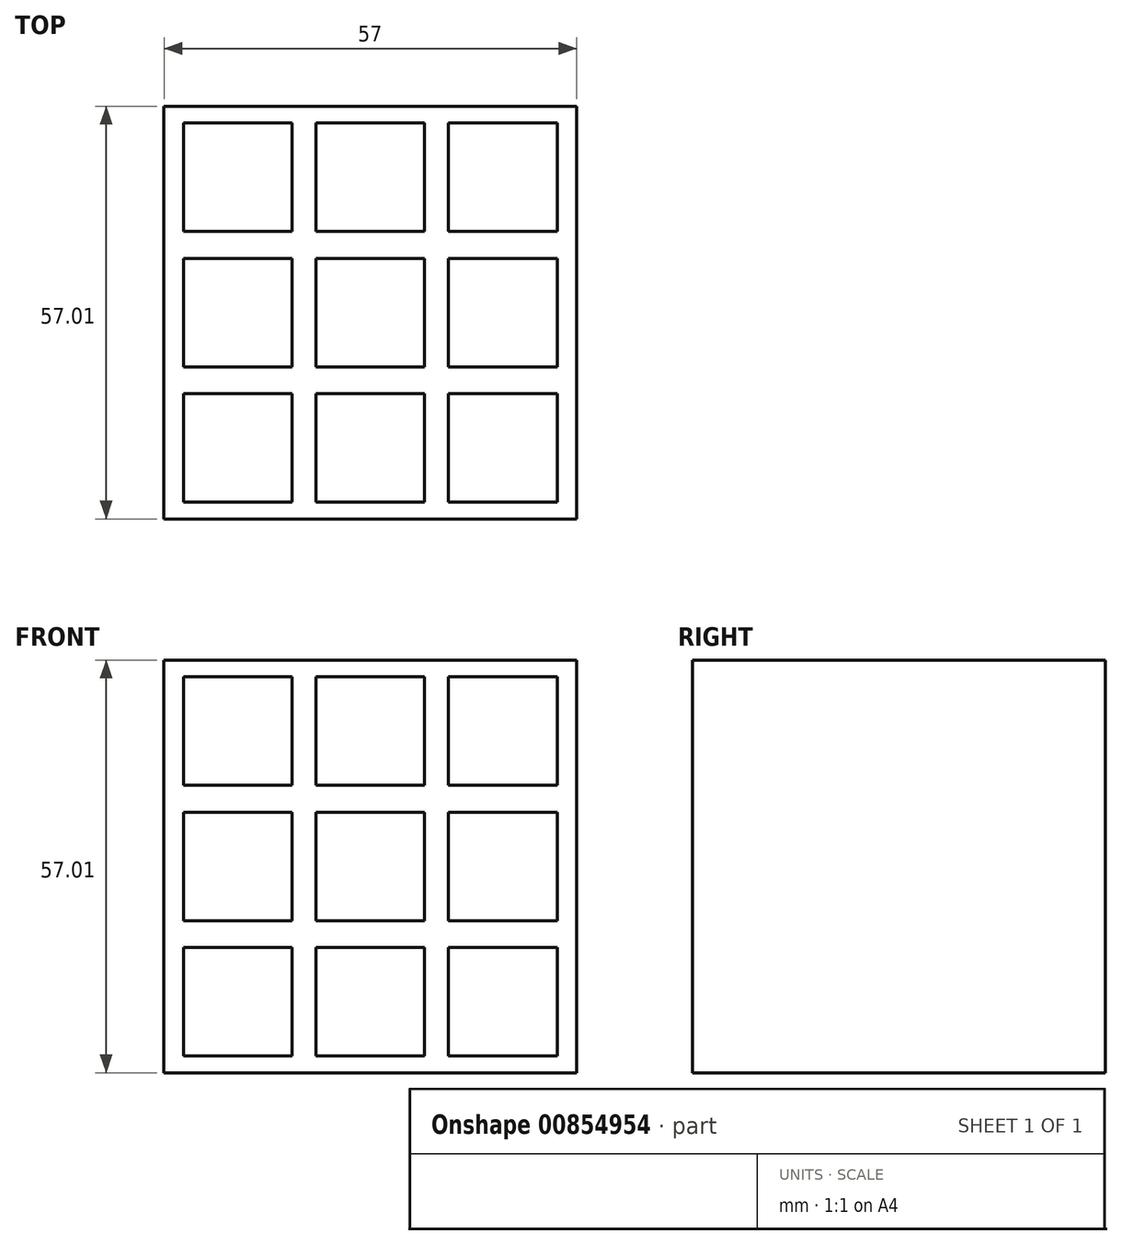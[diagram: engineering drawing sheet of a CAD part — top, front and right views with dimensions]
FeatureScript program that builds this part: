
annotation { "Feature Type Name" : "Feature", "Feature Type Description" : "" }
export const myFeature = defineFeature(function(context is Context, id is Id, definition is map)
    precondition{}
    {
        {
            var Q0;
            Q0=qCreatedBy(makeId("Front.planeOp"),FACE);
            var sketch = newSketch(context, id + "F0", { "sketchPlane" : qUnion([Q0])});
            skLineSegment(sketch, "E0.bottom", {"start": v(-57.56, 22.9) * mm, "end": v(-0.56, 22.9) * mm});
            skLineSegment(sketch, "E0.top", {"start": v(-57.56, -34.1) * mm, "end": v(-0.56, -34.1) * mm});
            skLineSegment(sketch, "E0.left", {"start": v(-57.56, 22.9) * mm, "end": v(-57.56, -34.1) * mm});
            skLineSegment(sketch, "E0.right", {"start": v(-0.56, 22.9) * mm, "end": v(-0.56, -34.1) * mm});
            skSolve(sketch);
        }
        {
            var Q0;
            Q0=qSketchRegion(id+"F0",true);
            extrude(context, id + "F1", {"entities" : qUnion([Q0]), "depth" : 57 * mm, "offsetDistance" : 25 * mm});
        }
        {
            var Q0;
            Q0=makeQuery(id+"F1.opExtrude","SWEPT_FACE",FACE,{"disambiguationData":[OSD([sQuery(id+"F0.wireOp",EDGE,"E0.bottom")])]});
            var sketch = newSketch(context, id + "F2", { "sketchPlane" : qUnion([Q0])});
            skLineSegment(sketch, "E1.bottom", {"start": v(-3.26, -2.3) * mm, "end": v(-18.26, -2.3) * mm});
            skLineSegment(sketch, "E1.top", {"start": v(-3.26, -17.3) * mm, "end": v(-18.26, -17.3) * mm});
            skLineSegment(sketch, "E1.left", {"start": v(-3.26, -2.3) * mm, "end": v(-3.26, -17.3) * mm});
            skLineSegment(sketch, "E1.right", {"start": v(-18.26, -2.3) * mm, "end": v(-18.26, -17.3) * mm});
            skLineSegment(sketch, "E2.bottom", {"start": v(-3.26, -21) * mm, "end": v(-18.26, -21) * mm});
            skLineSegment(sketch, "E2.top", {"start": v(-3.26, -36) * mm, "end": v(-18.26, -36) * mm});
            skLineSegment(sketch, "E2.left", {"start": v(-3.26, -21) * mm, "end": v(-3.26, -36) * mm});
            skLineSegment(sketch, "E2.right", {"start": v(-18.26, -21) * mm, "end": v(-18.26, -36) * mm});
            skLineSegment(sketch, "E3.bottom", {"start": v(-3.26, -39.7) * mm, "end": v(-18.26, -39.7) * mm});
            skLineSegment(sketch, "E3.top", {"start": v(-3.26, -54.7) * mm, "end": v(-18.26, -54.7) * mm});
            skLineSegment(sketch, "E3.left", {"start": v(-3.26, -39.7) * mm, "end": v(-3.26, -54.7) * mm});
            skLineSegment(sketch, "E3.right", {"start": v(-18.26, -39.7) * mm, "end": v(-18.26, -54.7) * mm});
            skLineSegment(sketch, "E4", {"start": v(-19.91, -57) * mm, "end": v(-19.91, 0) * mm});
            skLineSegment(sketch, "E5.MirrorCS", {"start": v(-36.56, -39.7) * mm, "end": v(-21.56, -39.7) * mm});
            skLineSegment(sketch, "E6.MirrorCS", {"start": v(-21.56, -39.7) * mm, "end": v(-21.56, -54.7) * mm});
            skLineSegment(sketch, "E7.MirrorCS", {"start": v(-36.56, -54.7) * mm, "end": v(-21.56, -54.7) * mm});
            skLineSegment(sketch, "E8.MirrorCS", {"start": v(-36.56, -39.7) * mm, "end": v(-36.56, -54.7) * mm});
            skLineSegment(sketch, "E9.MirrorCS", {"start": v(-36.56, -36) * mm, "end": v(-21.56, -36) * mm});
            skLineSegment(sketch, "E10.MirrorCS", {"start": v(-21.56, -21) * mm, "end": v(-21.56, -36) * mm});
            skLineSegment(sketch, "E11.MirrorCS", {"start": v(-36.56, -21) * mm, "end": v(-21.56, -21) * mm});
            skLineSegment(sketch, "E12.MirrorCS", {"start": v(-36.56, -21) * mm, "end": v(-36.56, -36) * mm});
            skLineSegment(sketch, "E13.MirrorCS", {"start": v(-36.56, -17.3) * mm, "end": v(-21.56, -17.3) * mm});
            skLineSegment(sketch, "E14.MirrorCS", {"start": v(-21.56, -2.3) * mm, "end": v(-21.56, -17.3) * mm});
            skLineSegment(sketch, "E15.MirrorCS", {"start": v(-36.56, -2.3) * mm, "end": v(-21.56, -2.3) * mm});
            skLineSegment(sketch, "E16.MirrorCS", {"start": v(-36.56, -2.3) * mm, "end": v(-36.56, -17.3) * mm});
            skLineSegment(sketch, "E17", {"start": v(-38.21, 0) * mm, "end": v(-38.21, -57) * mm});
            skLineSegment(sketch, "E18.MirrorCS", {"start": v(-39.86, -54.7) * mm, "end": v(-54.86, -54.7) * mm});
            skLineSegment(sketch, "E19.MirrorCS", {"start": v(-39.86, -39.7) * mm, "end": v(-39.86, -54.7) * mm});
            skLineSegment(sketch, "E20.MirrorCS", {"start": v(-39.86, -39.7) * mm, "end": v(-54.86, -39.7) * mm});
            skLineSegment(sketch, "E21.MirrorCS", {"start": v(-54.86, -39.7) * mm, "end": v(-54.86, -54.7) * mm});
            skLineSegment(sketch, "E22.MirrorCS", {"start": v(-39.86, -36) * mm, "end": v(-54.86, -36) * mm});
            skLineSegment(sketch, "E23.MirrorCS", {"start": v(-39.86, -21) * mm, "end": v(-54.86, -21) * mm});
            skLineSegment(sketch, "E24.MirrorCS", {"start": v(-39.86, -21) * mm, "end": v(-39.86, -36) * mm});
            skLineSegment(sketch, "E25.MirrorCS", {"start": v(-54.86, -21) * mm, "end": v(-54.86, -36) * mm});
            skLineSegment(sketch, "E26.MirrorCS", {"start": v(-39.86, -17.3) * mm, "end": v(-54.86, -17.3) * mm});
            skLineSegment(sketch, "E27.MirrorCS", {"start": v(-39.86, -2.3) * mm, "end": v(-54.86, -2.3) * mm});
            skLineSegment(sketch, "E28.MirrorCS", {"start": v(-54.86, -2.3) * mm, "end": v(-54.86, -17.3) * mm});
            skLineSegment(sketch, "E29.MirrorCS", {"start": v(-39.86, -2.3) * mm, "end": v(-39.86, -17.3) * mm});
            skSolve(sketch);
        }
        {
            var Q0;
            Q0=qSketchRegion(id+"F2",true);
            extrude(context, id + "F3", {"entities" : qUnion([Q0]), "operationType" : NewBodyOperationType.ADD, "depth" : 0.01 * mm, "offsetDistance" : 25 * mm});
        }
        {
            var Q0;
            Q0=makeQuery(id+"F1.opExtrude","CAP_FACE",FACE,{"disambiguationData":[OSD([sQuery(id+"F0.wireOp",EDGE,"E0.bottom"),sQuery(id+"F0.wireOp",EDGE,"E0.top"),sQuery(id+"F0.wireOp",EDGE,"E0.left"),sQuery(id+"F0.wireOp",EDGE,"E0.right")])],"isStart":false});
            var sketch = newSketch(context, id + "F4", { "sketchPlane" : qUnion([Q0])});
            skLineSegment(sketch, "E30.bottom", {"start": v(-3.26, 20.6) * mm, "end": v(-18.26, 20.6) * mm});
            skLineSegment(sketch, "E30.top", {"start": v(-3.26, 5.6) * mm, "end": v(-18.26, 5.6) * mm});
            skLineSegment(sketch, "E30.left", {"start": v(-3.26, 20.6) * mm, "end": v(-3.26, 5.6) * mm});
            skLineSegment(sketch, "E30.right", {"start": v(-18.26, 20.6) * mm, "end": v(-18.26, 5.6) * mm});
            skLineSegment(sketch, "E31.bottom", {"start": v(-3.26, 1.9) * mm, "end": v(-18.26, 1.9) * mm});
            skLineSegment(sketch, "E31.top", {"start": v(-3.26, -13.1) * mm, "end": v(-18.26, -13.1) * mm});
            skLineSegment(sketch, "E31.left", {"start": v(-3.26, 1.9) * mm, "end": v(-3.26, -13.1) * mm});
            skLineSegment(sketch, "E31.right", {"start": v(-18.26, 1.9) * mm, "end": v(-18.26, -13.1) * mm});
            skLineSegment(sketch, "E32.bottom", {"start": v(-3.26, -16.8) * mm, "end": v(-18.26, -16.8) * mm});
            skLineSegment(sketch, "E32.top", {"start": v(-3.26, -31.8) * mm, "end": v(-18.26, -31.8) * mm});
            skLineSegment(sketch, "E32.left", {"start": v(-3.26, -16.8) * mm, "end": v(-3.26, -31.8) * mm});
            skLineSegment(sketch, "E32.right", {"start": v(-18.26, -16.8) * mm, "end": v(-18.26, -31.8) * mm});
            skLineSegment(sketch, "E33", {"start": v(-19.91, -46.05) * mm, "end": v(-19.91, 10.95) * mm});
            skLineSegment(sketch, "E34.MirrorCS", {"start": v(-36.56, -16.8) * mm, "end": v(-21.56, -16.8) * mm});
            skLineSegment(sketch, "E35.MirrorCS", {"start": v(-21.56, -16.8) * mm, "end": v(-21.56, -31.8) * mm});
            skLineSegment(sketch, "E36.MirrorCS", {"start": v(-36.56, -31.8) * mm, "end": v(-21.56, -31.8) * mm});
            skLineSegment(sketch, "E37.MirrorCS", {"start": v(-36.56, -16.8) * mm, "end": v(-36.56, -31.8) * mm});
            skLineSegment(sketch, "E38.MirrorCS", {"start": v(-36.56, -13.1) * mm, "end": v(-21.56, -13.1) * mm});
            skLineSegment(sketch, "E39.MirrorCS", {"start": v(-21.56, 1.9) * mm, "end": v(-21.56, -13.1) * mm});
            skLineSegment(sketch, "E40.MirrorCS", {"start": v(-36.56, 1.9) * mm, "end": v(-21.56, 1.9) * mm});
            skLineSegment(sketch, "E41.MirrorCS", {"start": v(-36.56, 1.9) * mm, "end": v(-36.56, -13.1) * mm});
            skLineSegment(sketch, "E42.MirrorCS", {"start": v(-36.56, 5.6) * mm, "end": v(-21.56, 5.6) * mm});
            skLineSegment(sketch, "E43.MirrorCS", {"start": v(-21.56, 20.6) * mm, "end": v(-21.56, 5.6) * mm});
            skLineSegment(sketch, "E44.MirrorCS", {"start": v(-36.56, 20.6) * mm, "end": v(-21.56, 20.6) * mm});
            skLineSegment(sketch, "E45.MirrorCS", {"start": v(-36.56, 20.6) * mm, "end": v(-36.56, 5.6) * mm});
            skLineSegment(sketch, "E46", {"start": v(-38.21, 22.9) * mm, "end": v(-38.21, -46.05) * mm});
            skLineSegment(sketch, "E47.MirrorCS", {"start": v(-39.86, -31.8) * mm, "end": v(-54.86, -31.8) * mm});
            skLineSegment(sketch, "E48.MirrorCS", {"start": v(-39.86, -16.8) * mm, "end": v(-39.86, -31.8) * mm});
            skLineSegment(sketch, "E49.MirrorCS", {"start": v(-39.86, -16.8) * mm, "end": v(-54.86, -16.8) * mm});
            skLineSegment(sketch, "E50.MirrorCS", {"start": v(-54.86, -16.8) * mm, "end": v(-54.86, -31.8) * mm});
            skLineSegment(sketch, "E51.MirrorCS", {"start": v(-39.86, -13.1) * mm, "end": v(-54.86, -13.1) * mm});
            skLineSegment(sketch, "E52.MirrorCS", {"start": v(-39.86, 1.9) * mm, "end": v(-54.86, 1.9) * mm});
            skLineSegment(sketch, "E53.MirrorCS", {"start": v(-39.86, 1.9) * mm, "end": v(-39.86, -13.1) * mm});
            skLineSegment(sketch, "E54.MirrorCS", {"start": v(-54.86, 1.9) * mm, "end": v(-54.86, -13.1) * mm});
            skLineSegment(sketch, "E55.MirrorCS", {"start": v(-39.86, 5.6) * mm, "end": v(-54.86, 5.6) * mm});
            skLineSegment(sketch, "E56.MirrorCS", {"start": v(-39.86, 20.6) * mm, "end": v(-54.86, 20.6) * mm});
            skLineSegment(sketch, "E57.MirrorCS", {"start": v(-54.86, 20.6) * mm, "end": v(-54.86, 5.6) * mm});
            skLineSegment(sketch, "E58.MirrorCS", {"start": v(-39.86, 20.6) * mm, "end": v(-39.86, 5.6) * mm});
            skSolve(sketch);
        }
        {
            var Q0;
            Q0=qSketchRegion(id+"F4",true);
            extrude(context, id + "F5", {"entities" : qUnion([Q0]), "operationType" : NewBodyOperationType.ADD, "depth" : 0.01 * mm, "offsetDistance" : 25 * mm});
        }
    });
